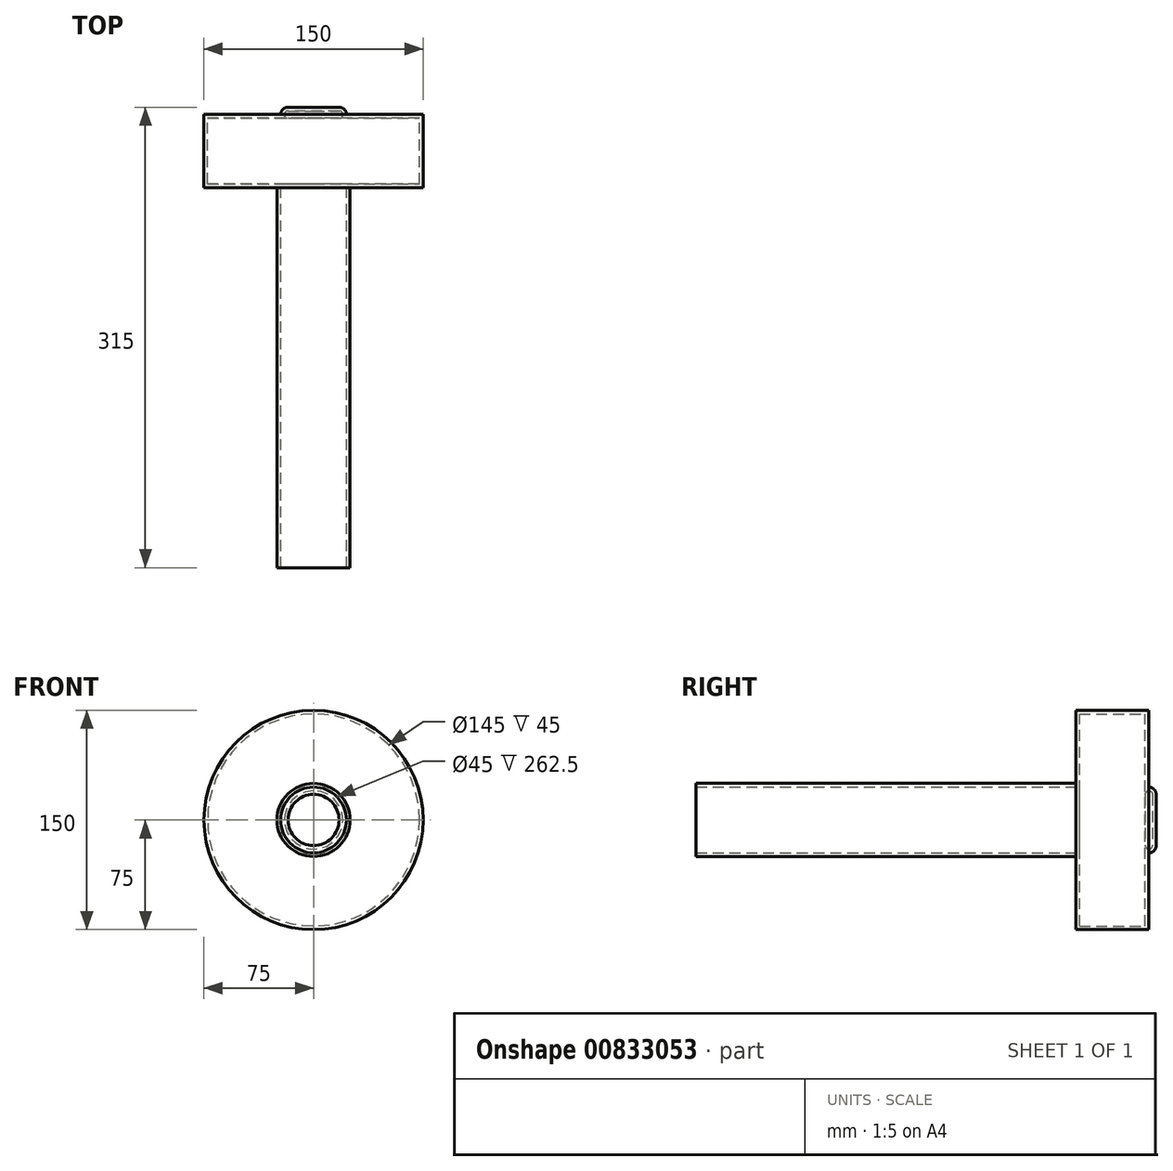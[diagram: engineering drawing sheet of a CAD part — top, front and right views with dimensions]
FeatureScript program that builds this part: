
annotation { "Feature Type Name" : "Feature", "Feature Type Description" : "" }
export const myFeature = defineFeature(function(context is Context, id is Id, definition is map)
    precondition{}
    {
        {
            var Q0;
            Q0=qCreatedBy(makeId("Front.planeOp"),FACE);
            var sketch = newSketch(context, id + "F0", { "sketchPlane" : qUnion([Q0])});
            skCircle(sketch, "E0", {"center": v(0, 0) * mm, "radius": 75 * mm});
            skSolve(sketch);
        }
        {
            var Q0;
            Q0=makeQuery(id+"F0.imprint","IMPRINT",FACE,{"disambiguationData":[TD([[makeQuery(id+"F0.imprint","IMPRINT",EDGE,{"derivedFrom":sQuery(id+"F0.wireOp",EDGE,"E0")}),1.0]])]});
            extrude(context, id + "F1", {"entities" : qUnion([Q0]), "depth" : 50 * mm, "offsetDistance" : 25 * mm});
        }
        {
            var Q0;
            Q0=makeQuery(id+"F1.opExtrude","CAP_FACE",FACE,{"disambiguationData":[OSD([sQuery(id+"F0.wireOp",EDGE,"E0")])],"isStart":false});
            var sketch = newSketch(context, id + "F2", { "sketchPlane" : qUnion([Q0])});
            skCircle(sketch, "E1", {"center": v(0, 0) * mm, "radius": 25 * mm});
            skSolve(sketch);
        }
        {
            var Q0;
            Q0=makeQuery(id+"F2.imprint","IMPRINT",FACE,{"disambiguationData":[TD([[makeQuery(id+"F2.imprint","IMPRINT",EDGE,{"derivedFrom":sQuery(id+"F2.wireOp",EDGE,"E1")}),1.0]])]});
            extrude(context, id + "F3", {"entities" : qUnion([Q0]), "operationType" : NewBodyOperationType.ADD, "depth" : 260 * mm, "offsetDistance" : 25 * mm});
        }
        {
            var Q0;
            Q0=makeQuery(id+"F1.opExtrude","CAP_FACE",FACE,{"disambiguationData":[OSD([sQuery(id+"F0.wireOp",EDGE,"E0")])],"isStart":true});
            var sketch = newSketch(context, id + "F4", { "sketchPlane" : qUnion([Q0])});
            skCircle(sketch, "E2", {"center": v(0, 0) * mm, "radius": 22.5 * mm});
            skSolve(sketch);
        }
        {
            var Q0;
            Q0=makeQuery(id+"F4.imprint","IMPRINT",FACE,{"disambiguationData":[TD([[makeQuery(id+"F4.imprint","IMPRINT",EDGE,{"derivedFrom":sQuery(id+"F4.wireOp",EDGE,"E2")}),1.0]])]});
            extrude(context, id + "F5", {"entities" : qUnion([Q0]), "operationType" : NewBodyOperationType.ADD, "depth" : 5 * mm, "offsetDistance" : 25 * mm});
        }
        {
            var Q0;
            Q0=makeQuery(id+"F5.opExtrude","CAP_FACE",FACE,{"disambiguationData":[OSD([sQuery(id+"F4.wireOp",EDGE,"E2")])],"isStart":false});
            fillet(context, id + "F6", {"entities" : qUnion([Q0]), "radius" : 5 * mm, "tangentPropagation" : true, "allowEdgeOverflow" : false});
        }
        {
            var Q0;
            Q0=makeQuery(id+"F3.opExtrude","CAP_FACE",FACE,{"disambiguationData":[OSD([sQuery(id+"F2.wireOp",EDGE,"E1")])],"isStart":false});
            shell(context, id + "F7", {"entities" : qUnion([Q0]), "thickness" : 2.5 * mm});
        }
    });
